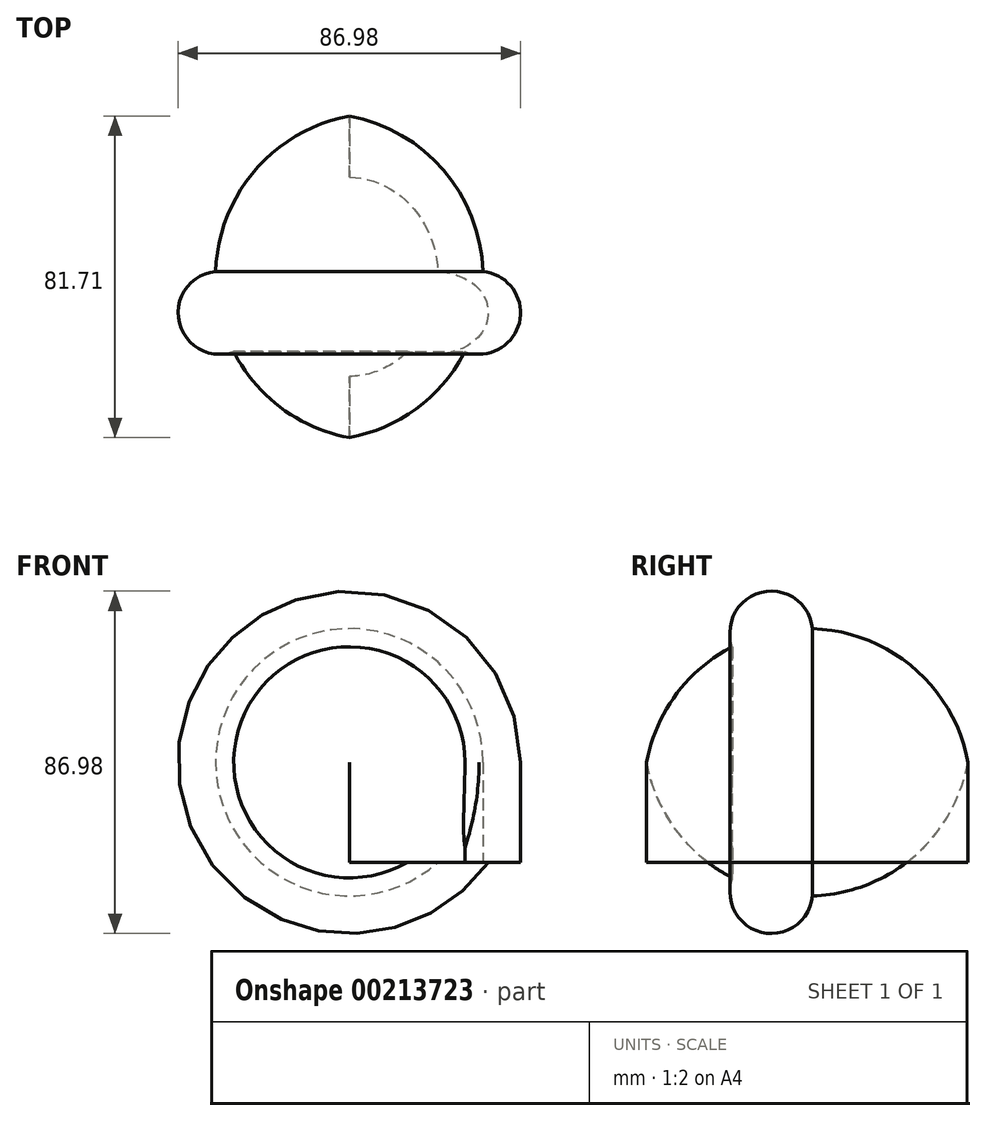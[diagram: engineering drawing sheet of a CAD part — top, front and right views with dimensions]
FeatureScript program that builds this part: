
annotation { "Feature Type Name" : "Feature", "Feature Type Description" : "" }
export const myFeature = defineFeature(function(context is Context, id is Id, definition is map)
    precondition{}
    {
        {
            var Q0;
            Q0=qCreatedBy(makeId("Top.planeOp"),FACE);
            var sketch = newSketch(context, id + "F0", { "sketchPlane" : qUnion([Q0])});
            skLineSegment(sketch, "E0", {"start": v(0, 36.7) * mm, "end": v(0, -45) * mm});
            skArc(sketch, "E1", {"start": v(0, -45) * mm, "mid": v(17.21, -37.5) * mm, "end": v(29.36, -23.2) * mm});
            skArc(sketch, "E2", {"start": v(29.36, -23.2) * mm, "mid": v(43.23, -15.61) * mm, "end": v(33.96, -2.81) * mm});
            skArc(sketch, "E3.trimOffspring", {"start": v(33.96, -2.81) * mm, "mid": v(23.94, 22.93) * mm, "end": v(0, 36.7) * mm});
            skSolve(sketch);
        }
        {
            var Q0;
            Q0 = qSketchRegion(id + "F0", true);
            extrude(context, id + "F1", {"entities" : qUnion([Q0]), "depth" : 25.4 * mm});
        }
        {
            var Q0;
            Q0=makeQuery(id+"F1.opExtrude","CAP_FACE",FACE,{"disambiguationData":[OSD([sQuery(id+"F0.wireOp",EDGE,"E0"),sQuery(id+"F0.wireOp",EDGE,"E1"),sQuery(id+"F0.wireOp",EDGE,"E2"),sQuery(id+"F0.wireOp",EDGE,"E3.trimOffspring")])],"isStart":false});
            var Q1;
            Q1=makeQuery(id+"F1.opExtrude","CAP_EDGE",EDGE,{"disambiguationData":[OSD([sQuery(id+"F0.wireOp",EDGE,"E0")])],"isStart":false});
            revolve(context, id + "F2", {"operationType" : NewBodyOperationType.ADD, "entities" : qUnion([Q0]), "axis" : qUnion([Q1]), "revolveType" : RevolveType.FULL});
        }
    });
